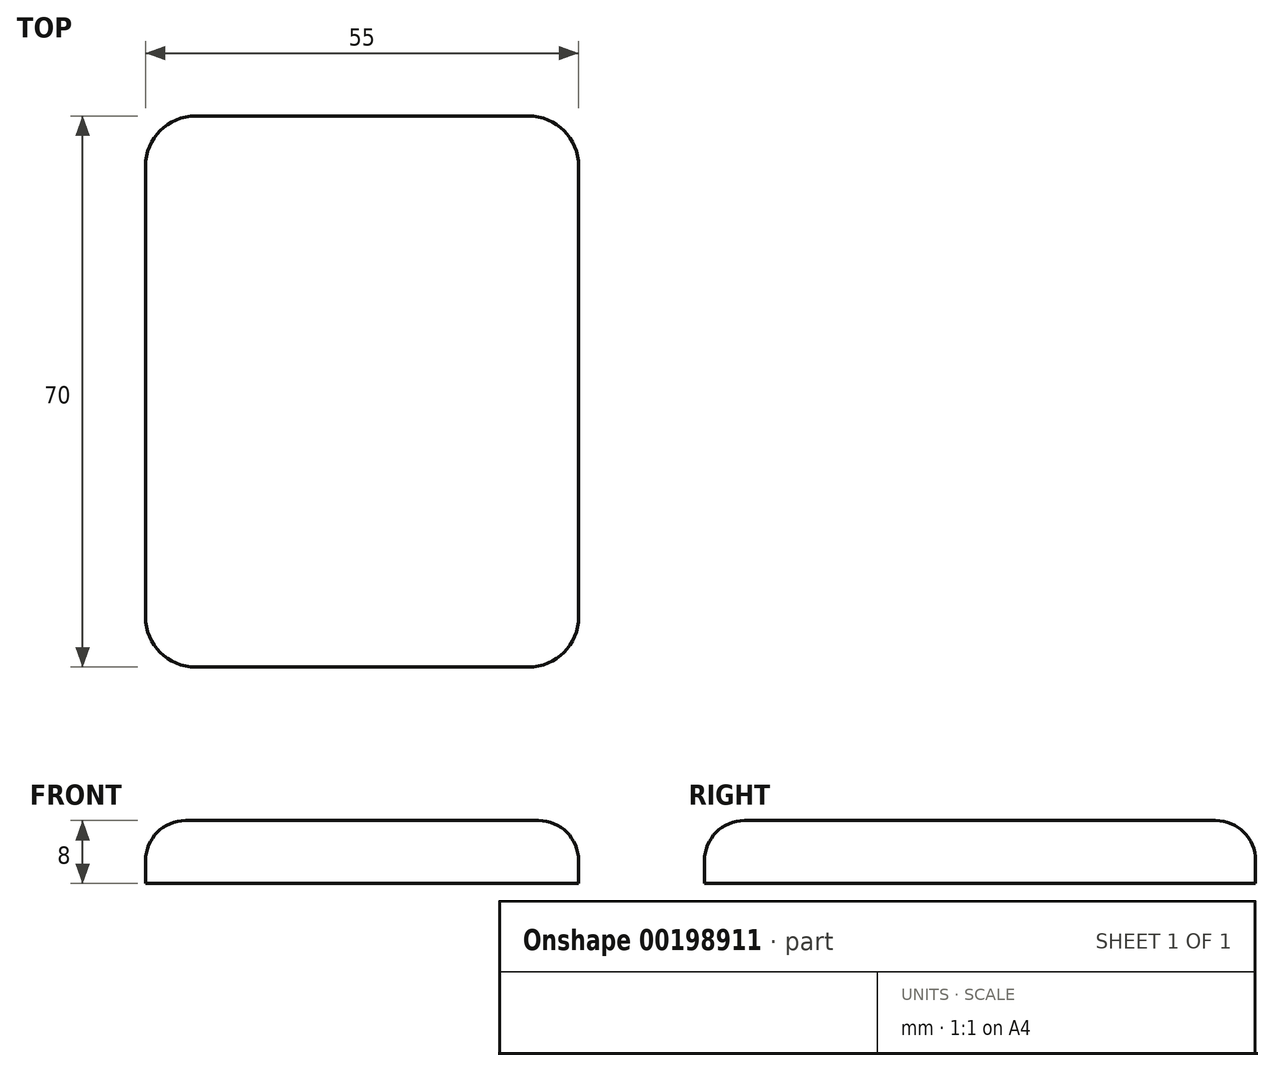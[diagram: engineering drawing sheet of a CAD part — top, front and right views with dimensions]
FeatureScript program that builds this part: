
annotation { "Feature Type Name" : "Feature", "Feature Type Description" : "" }
export const myFeature = defineFeature(function(context is Context, id is Id, definition is map)
    precondition{}
    {
        {
            var Q0;
            Q0=qCreatedBy(makeId("Front.planeOp"),FACE);
            var sketch = newSketch(context, id + "F0", { "sketchPlane" : qUnion([Q0])});
            skLineSegment(sketch, "E0.bottom", {"start": v(-27.5, -4) * mm, "end": v(27.5, -4) * mm});
            skLineSegment(sketch, "E0.top", {"start": v(-27.5, 4) * mm, "end": v(27.5, 4) * mm});
            skLineSegment(sketch, "E0.left", {"start": v(-27.5, -4) * mm, "end": v(-27.5, 4) * mm});
            skLineSegment(sketch, "E0.right", {"start": v(27.5, -4) * mm, "end": v(27.5, 4) * mm});
            skPoint(sketch, "E0.middle", {"position": v(0, 0) * mm});
            skSolve(sketch);
        }
        {
            var Q0;
            Q0 = qSketchRegion(id + "F0", true);
            extrude(context, id + "F1", {"entities" : qUnion([Q0]), "depth" : 70 * mm});
        }
        {
            var Q0;
            Q0=makeQuery(id+"F1.opExtrude","CAP_EDGE",EDGE,{"disambiguationData":[OSD([sQuery(id+"F0.wireOp",EDGE,"E0.left")])],"isStart":false});
            var Q1;
            Q1=makeQuery(id+"F1.opExtrude","CAP_EDGE",EDGE,{"disambiguationData":[OSD([sQuery(id+"F0.wireOp",EDGE,"E0.right")])],"isStart":false});
            var Q2;
            Q2=makeQuery(id+"F1.opExtrude","CAP_EDGE",EDGE,{"disambiguationData":[OSD([sQuery(id+"F0.wireOp",EDGE,"E0.right")])],"isStart":true});
            var Q3;
            Q3=makeQuery(id+"F1.opExtrude","CAP_EDGE",EDGE,{"disambiguationData":[OSD([sQuery(id+"F0.wireOp",EDGE,"E0.left")])],"isStart":true});
            fillet(context, id + "F2", {"entities" : qUnion([Q0, Q1, Q2, Q3]), "radius" : 6.35 * mm, "tangentPropagation" : true, "allowEdgeOverflow" : false});
        }
        {
            var Q0;
            Q0=makeQuery(id+"F1.opExtrude","SWEPT_FACE",FACE,{"disambiguationData":[OSD([sQuery(id+"F0.wireOp",EDGE,"E0.top")])]});
            fillet(context, id + "F3", {"entities" : qUnion([Q0]), "radius" : 5.08 * mm, "tangentPropagation" : true, "allowEdgeOverflow" : false});
        }
    });
